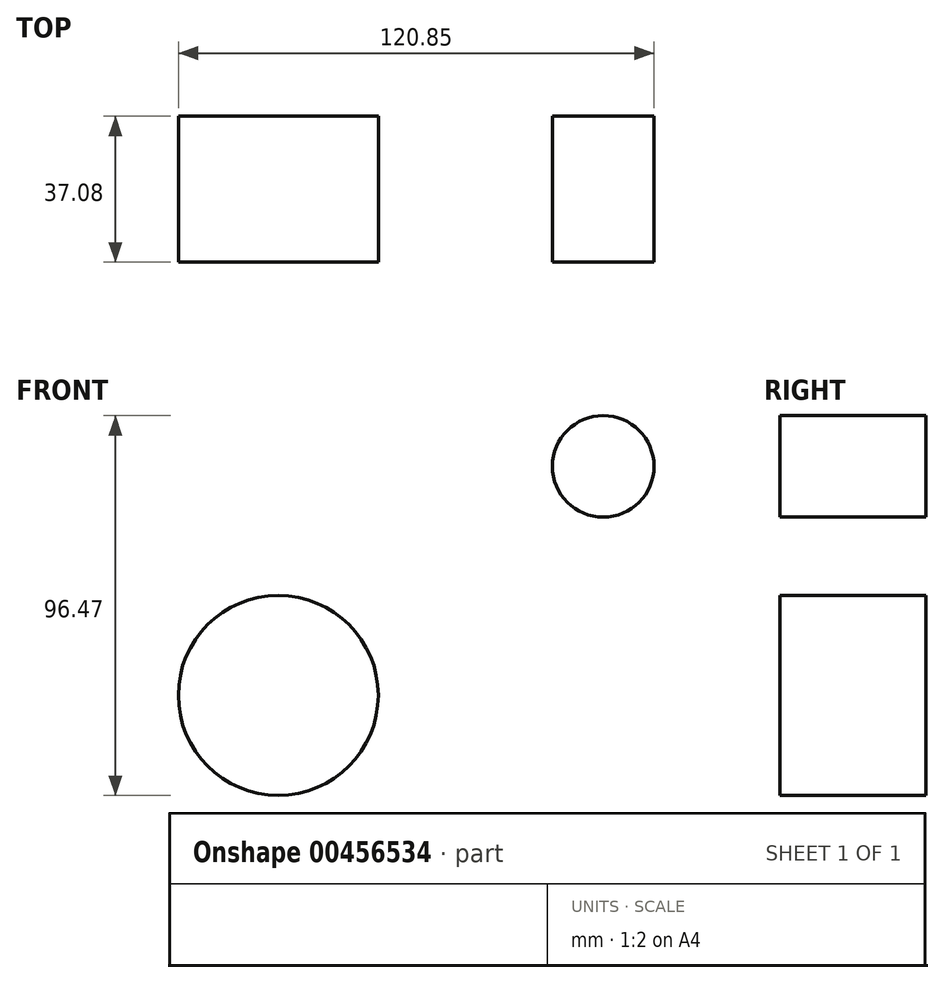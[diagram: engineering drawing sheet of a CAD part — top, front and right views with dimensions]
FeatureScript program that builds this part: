
annotation { "Feature Type Name" : "Feature", "Feature Type Description" : "" }
export const myFeature = defineFeature(function(context is Context, id is Id, definition is map)
    precondition{}
    {
        {
            var Q0;
            Q0=qCreatedBy(makeId("Front.planeOp"),FACE);
            var sketch = newSketch(context, id + "F0", { "sketchPlane" : qUnion([Q0])});
            skCircle(sketch, "E0", {"center": v(-47.9, 50.4) * mm, "radius": 12.9 * mm});
            skCircle(sketch, "E1", {"center": v(37.27, 49) * mm, "radius": 20.73 * mm});
            skSolve(sketch);
        }
        {
            var Q0;
            Q0=qCreatedBy(makeId("Front.planeOp"),FACE);
            var sketch = newSketch(context, id + "F1", { "sketchPlane" : qUnion([Q0])});
            skCircle(sketch, "E2", {"center": v(-130.44, -7.77) * mm, "radius": 25.4 * mm});
            skSolve(sketch);
        }
        {
            var Q0;
            Q0=makeQuery(id+"F1.imprint","IMPRINT",FACE,{"disambiguationData":[TD([[makeQuery(id+"F1.imprint","IMPRINT",EDGE,{"derivedFrom":sQuery(id+"F1.wireOp",EDGE,"E2")}),1.0]])]});
            var Q1;
            Q1=makeQuery(id+"F0.imprint","IMPRINT",FACE,{"disambiguationData":[TD([[makeQuery(id+"F0.imprint","IMPRINT",EDGE,{"derivedFrom":sQuery(id+"F0.wireOp",EDGE,"E0")}),1.0]])]});
            extrude(context, id + "F2", {"entities" : qUnion([Q0, Q1]), "depth" : 37.08 * mm});
        }
    });
